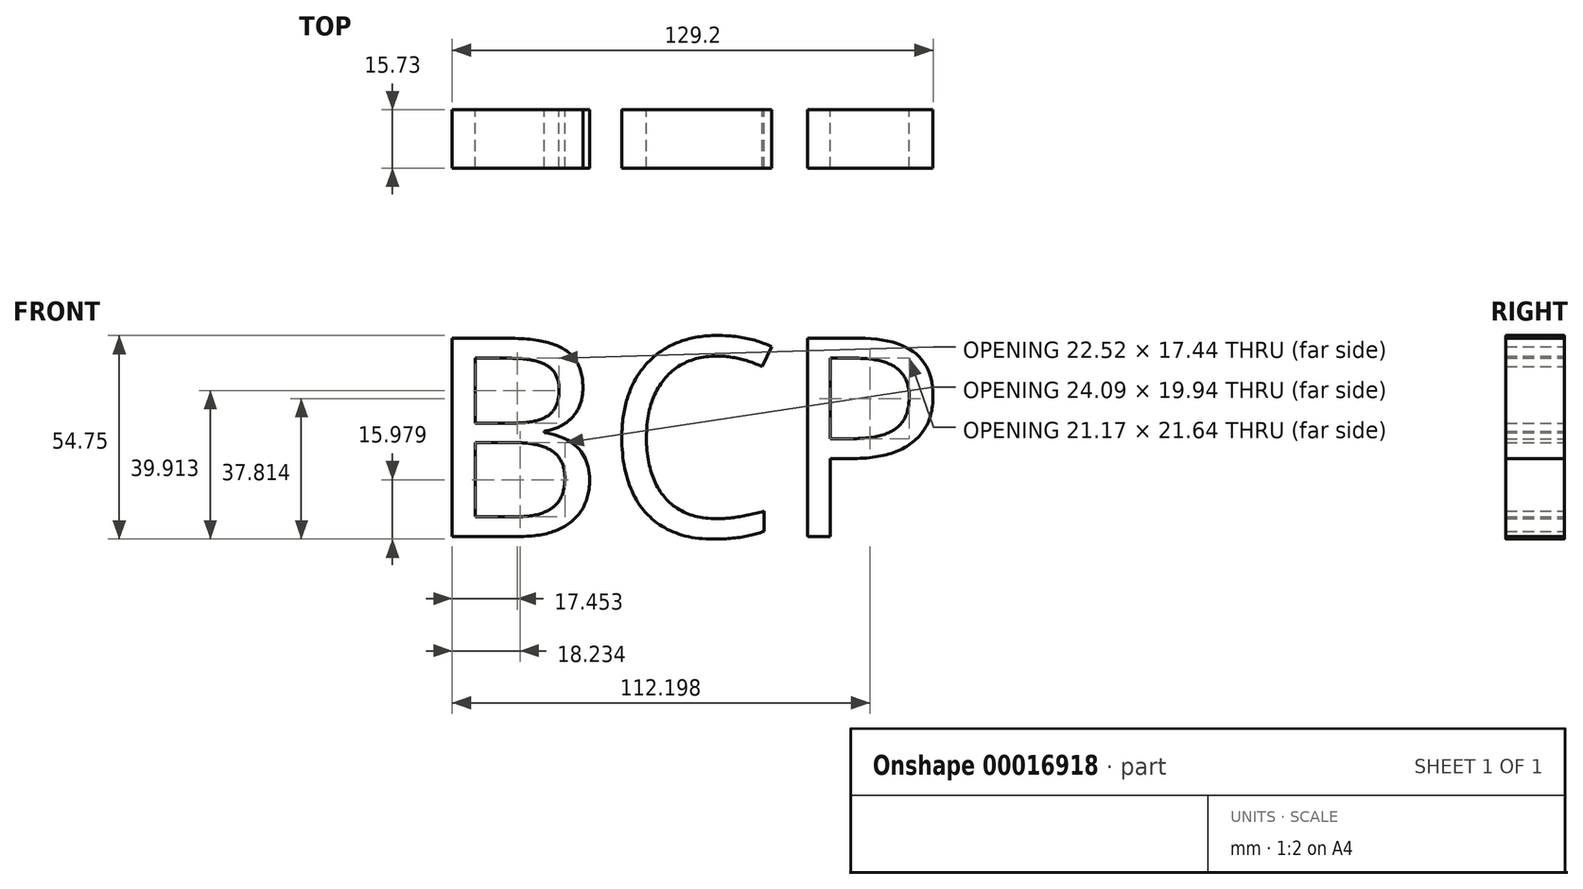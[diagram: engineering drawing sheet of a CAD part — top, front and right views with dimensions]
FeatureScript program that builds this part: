
annotation { "Feature Type Name" : "Feature", "Feature Type Description" : "" }
export const myFeature = defineFeature(function(context is Context, id is Id, definition is map)
    precondition{}
    {
        {
            var Q0;
            Q0=qCreatedBy(makeId("Front.planeOp"),FACE);
            var sketch = newSketch(context, id + "F0", { "sketchPlane" : qUnion([Q0])});
            skText(sketch, "E0", { "text": "BCP", "fontName": "OpenSans-Regular.ttf"});
            const initialGuessF0  = {"E0": [-0.04884, -0.0289, 1, 0, 0.05372]};
            skSetInitialGuess(sketch, initialGuessF0);
            skSolve(sketch);
        }
        {
            var Q0;
            Q0=makeQuery(id+"F0.imprint","IMPRINT",FACE,{"disambiguationData":[TD([[makeQuery(id+"F0.imprint","IMPRINT",EDGE,{"derivedFrom":sQuery(id+"F0.wireOp",EDGE,"E0.sketch_text.stroke-25")}),-1.0]])]});
            var Q1;
            Q1=makeQuery(id+"F0.imprint","IMPRINT",FACE,{"disambiguationData":[TD([[makeQuery(id+"F0.imprint","IMPRINT",EDGE,{"derivedFrom":sQuery(id+"F0.wireOp",EDGE,"E0.sketch_text.stroke-0")}),-1.0]])]});
            var Q2;
            Q2=makeQuery(id+"F0.imprint","IMPRINT",FACE,{"disambiguationData":[TD([[makeQuery(id+"F0.imprint","IMPRINT",EDGE,{"derivedFrom":sQuery(id+"F0.wireOp",EDGE,"E0.sketch_text.stroke-40")}),-1.0]])]});
            extrude(context, id + "F1", {"entities" : qUnion([Q0, Q1, Q2]), "depth" : 15.73 * mm});
        }
    });
